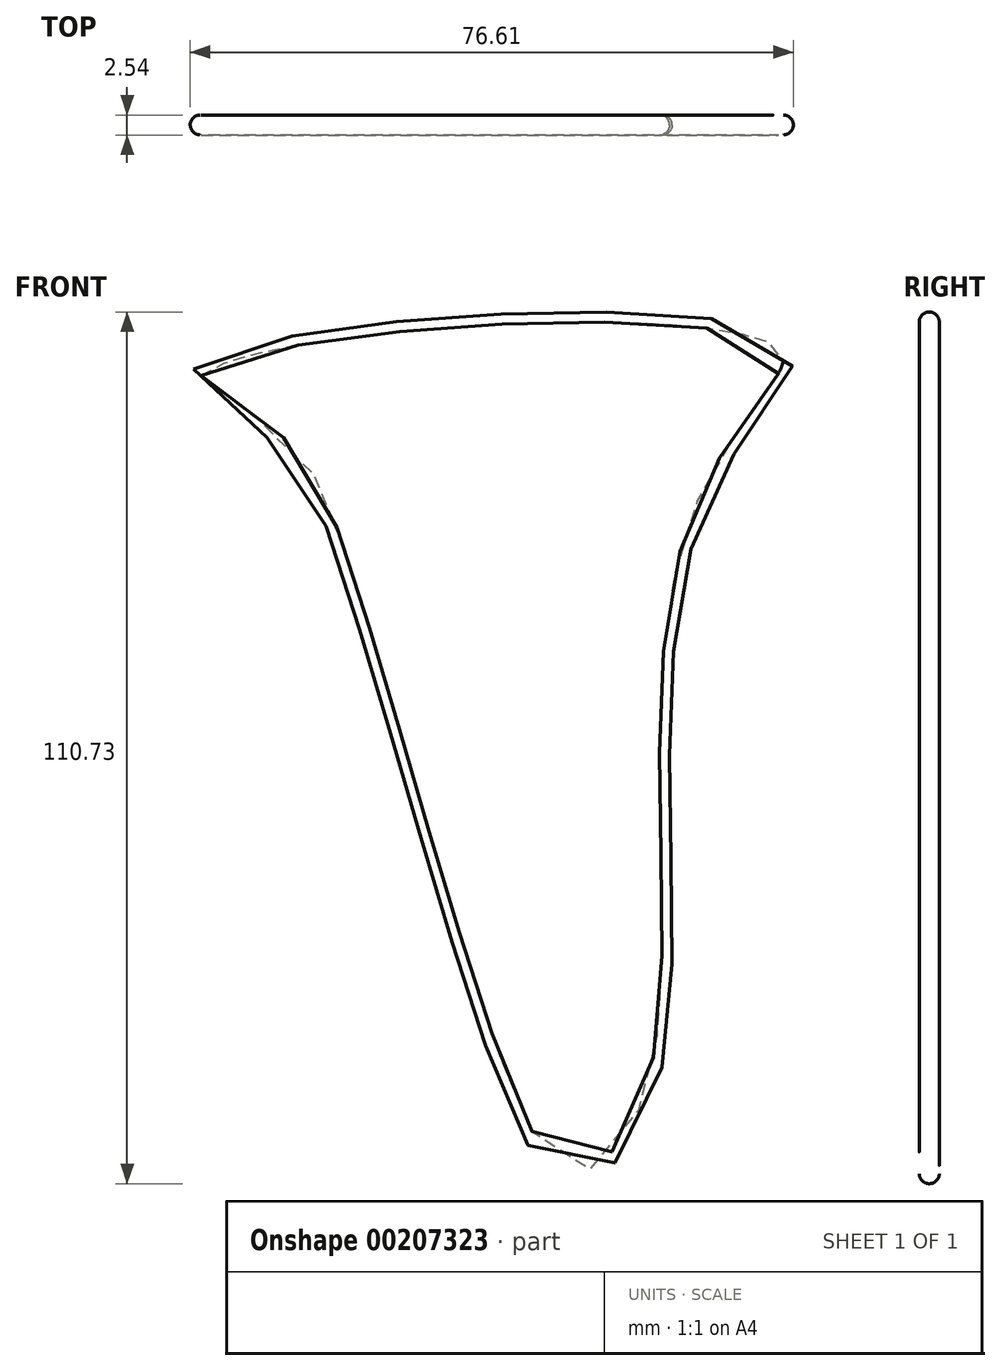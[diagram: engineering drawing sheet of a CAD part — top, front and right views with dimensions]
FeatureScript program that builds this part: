
annotation { "Feature Type Name" : "Feature", "Feature Type Description" : "" }
export const myFeature = defineFeature(function(context is Context, id is Id, definition is map)
    precondition{}
    {
        {
            var Q0;
            Q0=qCreatedBy(makeId("Front.planeOp"),FACE);
            var sketch = newSketch(context, id + "F0", { "sketchPlane" : qUnion([Q0])});
            skFitSpline(sketch, "E0", {"points": [v(-53.9, 43.52) * mm, v(-46.4, 36.01) * mm, v(-37.12, 23.64) * mm, v(-12.81, -52.36) * mm, v(-4.86, -59.87) * mm, v(3.98, -50.6) * mm, v(6.63, -12.6) * mm, v(13.7, 31.15) * mm, v(20.77, 47.5) * mm, v(-53.9, 43.52) * mm]});
            skSolve(sketch);
        }
        {
            var Q0;
            Q0=makeQuery(id+"F0.imprint","IMPRINT",FACE,{"disambiguationData":[TD([[makeQuery(id+"F0.imprint","IMPRINT",EDGE,{"derivedFrom":sQuery(id+"F0.wireOp",EDGE,"E0")}),1.0]])]});
            extrude(context, id + "F1", {"entities" : qUnion([Q0]), "depth" : 2.54 * mm});
        }
        {
            var Q0;
            Q0=makeQuery(id+"F1.opExtrude","CAP_EDGE",EDGE,{"disambiguationData":[OSD([sQuery(id+"F0.wireOp",EDGE,"E0")])],"isStart":false});
            var Q1;
            Q1=makeQuery(id+"F1.opExtrude","CAP_EDGE",EDGE,{"disambiguationData":[OSD([sQuery(id+"F0.wireOp",EDGE,"E0")])],"isStart":true});
            fillet(context, id + "F2", {"entities" : qUnion([Q0, Q1]), "radius" : 1.27 * mm, "tangentPropagation" : true, "allowEdgeOverflow" : false});
        }
    });
